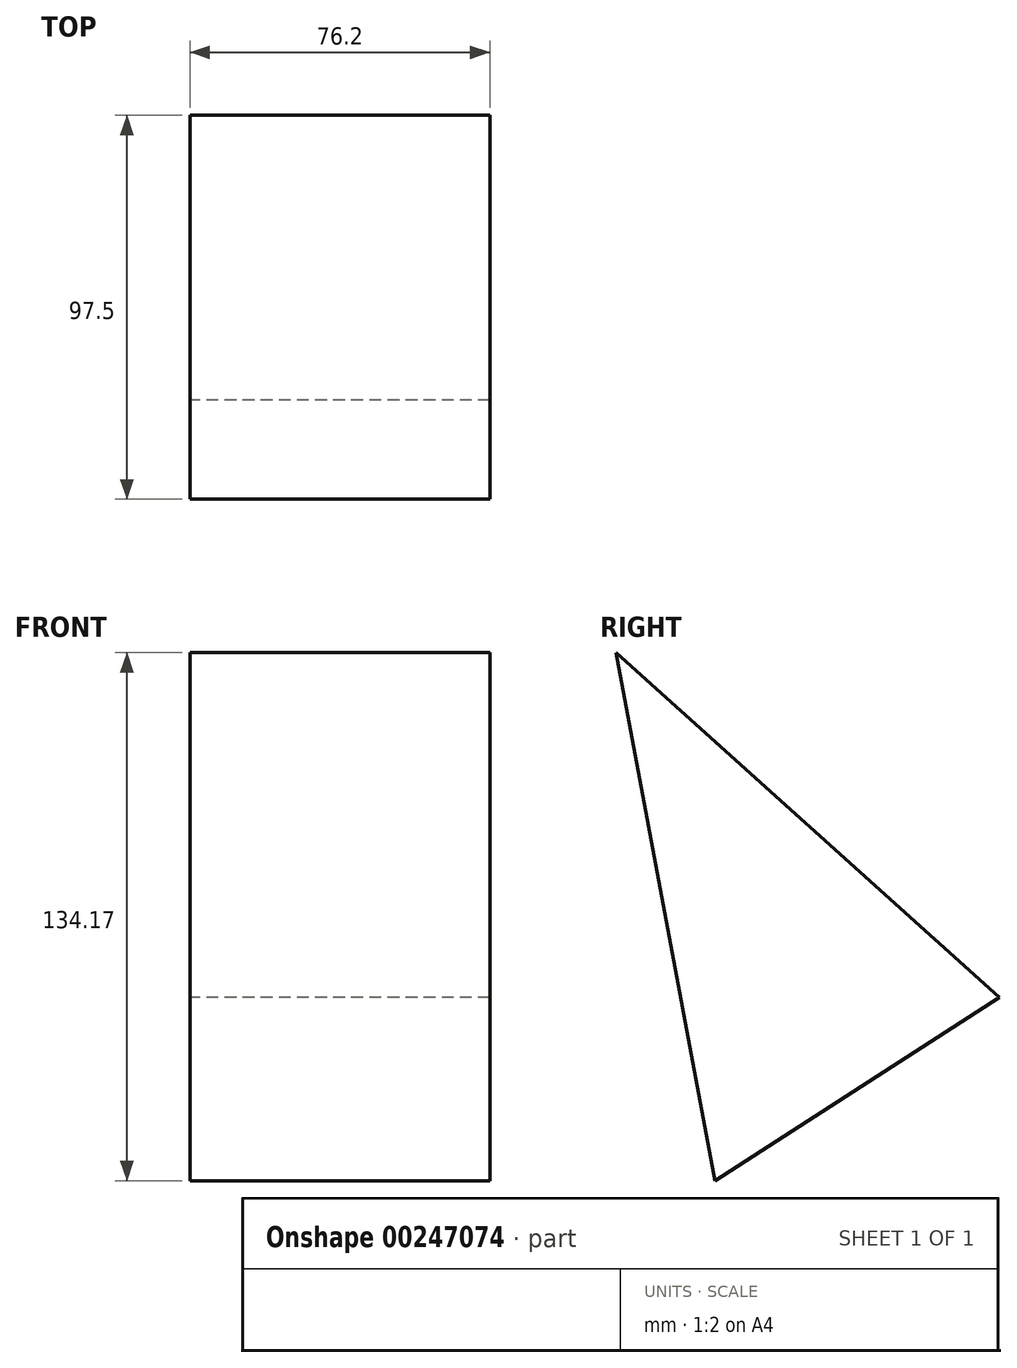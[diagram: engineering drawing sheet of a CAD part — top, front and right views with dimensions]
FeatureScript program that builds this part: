
annotation { "Feature Type Name" : "Feature", "Feature Type Description" : "" }
export const myFeature = defineFeature(function(context is Context, id is Id, definition is map)
    precondition{}
    {
        {
            var Q0;
            Q0=qCreatedBy(makeId("Right.planeOp"),FACE);
            var sketch = newSketch(context, id + "F0", { "sketchPlane" : qUnion([Q0])});
            skLineSegment(sketch, "E0", {"start": v(67.03, -23.01) * mm, "end": v(-30.47, 64.54) * mm});
            skLineSegment(sketch, "E1", {"start": v(-30.47, 64.54) * mm, "end": v(-5.26, -69.63) * mm});
            skLineSegment(sketch, "E2", {"start": v(-5.26, -69.63) * mm, "end": v(67.03, -23.01) * mm});
            skSolve(sketch);
        }
        {
            var Q0;
            Q0=makeQuery(id+"F0.imprint","IMPRINT",FACE,{"disambiguationData":[TD([[makeQuery(id+"F0.imprint","IMPRINT",EDGE,{"derivedFrom":sQuery(id+"F0.wireOp",EDGE,"E0")}),1.0]])]});
            extrude(context, id + "F1", {"entities" : qUnion([Q0]), "depth" : 76.2 * mm});
        }
    });
